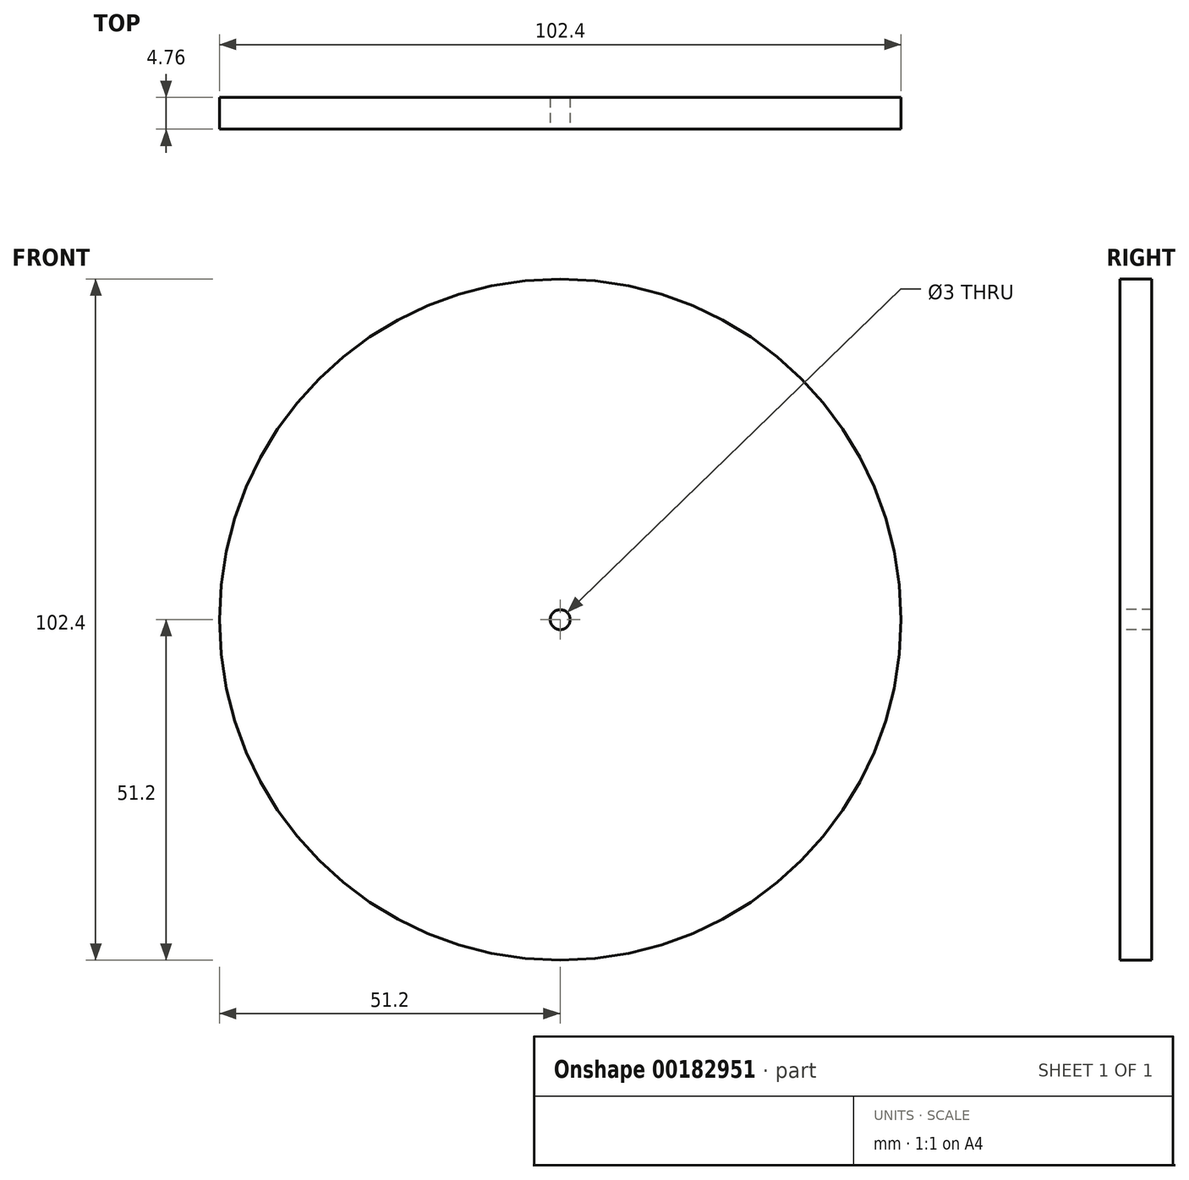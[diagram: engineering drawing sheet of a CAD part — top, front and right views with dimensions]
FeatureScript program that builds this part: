
annotation { "Feature Type Name" : "Feature", "Feature Type Description" : "" }
export const myFeature = defineFeature(function(context is Context, id is Id, definition is map)
    precondition{}
    {
        {
            var Q0;
            Q0=qCreatedBy(makeId("Front.planeOp"),FACE);
            var sketch = newSketch(context, id + "F0", { "sketchPlane" : qUnion([Q0])});
            skCircle(sketch, "E0", {"center": v(0, 0) * mm, "radius": 51.2 * mm});
            skCircle(sketch, "E1", {"center": v(0, 0) * mm, "radius": 1.5 * mm});
            skSolve(sketch);
        }
        {
            var Q0;
            Q0=makeQuery(id+"F0.imprint","IMPRINT",FACE,{"disambiguationData":[TD([[makeQuery(id+"F0.imprint","IMPRINT",EDGE,{"derivedFrom":sQuery(id+"F0.wireOp",EDGE,"E0")}),1.0]])]});
            var Q1;
            Q1=sQuery(id+"F0.wireOp",EDGE,"E1");
            var Q2;
            Q2=sQuery(id+"F0.wireOp",EDGE,"E0");
            extrude(context, id + "F1", {"entities" : qUnion([Q0]), "surfaceEntities" : qUnion([Q1, Q2]), "oppositeDirection" : true, "depth" : 4.76 * mm});
        }
    });
